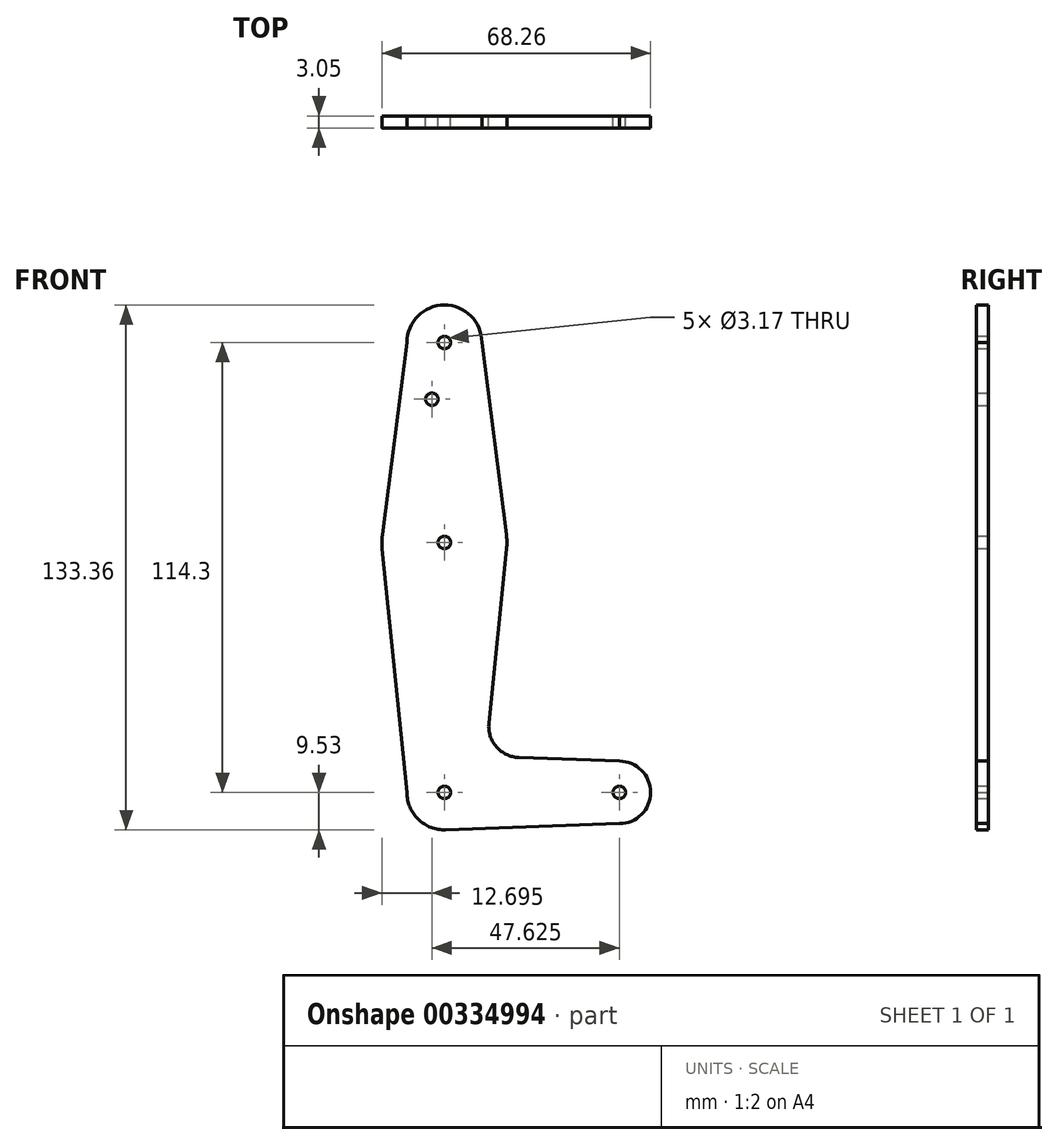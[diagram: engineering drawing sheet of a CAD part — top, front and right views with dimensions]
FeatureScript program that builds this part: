
annotation { "Feature Type Name" : "Feature", "Feature Type Description" : "" }
export const myFeature = defineFeature(function(context is Context, id is Id, definition is map)
    precondition{}
    {
        {
            var Q0;
            Q0=qCreatedBy(makeId("Front.planeOp"),FACE);
            var sketch = newSketch(context, id + "F0", { "sketchPlane" : qUnion([Q0])});
            skLineSegment(sketch, "E0", {"start": v(0, 0) * mm, "end": v(0, 114.3) * mm, "construction": true});
            skCircle(sketch, "E1", {"center": v(0, 114.3) * mm, "radius": 9.53 * mm});
            skCircle(sketch, "E2", {"center": v(0, 63.5) * mm, "radius": 15.88 * mm});
            skLineSegment(sketch, "E3", {"start": v(0, 0) * mm, "end": v(44.45, 0) * mm, "construction": true});
            skCircle(sketch, "E4", {"center": v(0, 0) * mm, "radius": 9.53 * mm});
            skCircle(sketch, "E5", {"center": v(44.45, 0) * mm, "radius": 7.94 * mm});
            skLineSegment(sketch, "E6", {"start": v(-9.53, 114.3) * mm, "end": v(-15.75, 65.5) * mm});
            skLineSegment(sketch, "E7", {"start": v(9.53, 114.3) * mm, "end": v(15.75, 65.5) * mm});
            skLineSegment(sketch, "E8", {"start": v(15.8, 61.9) * mm, "end": v(11.3, 17.6) * mm});
            skCircle(sketch, "E9", {"center": v(-3.18, 99.89) * mm, "radius": 1.59 * mm});
            skCircle(sketch, "E10", {"center": v(0, 114.3) * mm, "radius": 1.59 * mm});
            skCircle(sketch, "E11", {"center": v(0, 63.5) * mm, "radius": 1.59 * mm});
            skCircle(sketch, "E12", {"center": v(0, 0) * mm, "radius": 1.59 * mm});
            skCircle(sketch, "E13", {"center": v(44.45, 0) * mm, "radius": 1.59 * mm});
            skLineSegment(sketch, "E14", {"start": v(44.45, 7.94) * mm, "end": v(18.93, 8.85) * mm});
            skLineSegment(sketch, "E15", {"start": v(44.45, -7.94) * mm, "end": v(0, -9.53) * mm});
            skPoint(sketch, "E16.newPointA", {"position": v(9.53, 0) * mm});
            skArc(sketch, "E16.filletArc", {"start": v(11.3, 17.6) * mm, "mid": v(13.22, 11.57) * mm, "end": v(18.93, 8.85) * mm});
            skLineSegment(sketch, "E17", {"start": v(-15.8, 61.9) * mm, "end": v(-9.52, 0) * mm});
            skSolve(sketch);
        }
        {
            var Q0;
            {var subQ6=sQuery(id+"F0.wireOp",EDGE,"E8");Q0=makeQuery(id+"F0.imprint","IMPRINT",FACE,{"disambiguationData":[TD([[makeQuery(id+"F0.imprint","IMPRINT",EDGE,{"derivedFrom":subQ6}),-1.0]])]});}
            var Q1;
            {var subQ0=sQuery(id+"F0.wireOp",EDGE,"E6");Q1=makeQuery(id+"F0.imprint","IMPRINT",FACE,{"disambiguationData":[TD([[makeQuery(id+"F0.imprint","IMPRINT",EDGE,{"derivedFrom":subQ0}),1.0]])]});}
            var Q2;
            Q2=makeQuery(id+"F0.imprint","IMPRINT",FACE,{"disambiguationData":[TD([[makeQuery(id+"F0.imprint","IMPRINT",EDGE,{"derivedFrom":sQuery(id+"F0.wireOp",EDGE,"E11")}),-1.0]])]});
            var Q3;
            Q3=makeQuery(id+"F0.imprint","IMPRINT",FACE,{"disambiguationData":[TD([[makeQuery(id+"F0.imprint","IMPRINT",EDGE,{"derivedFrom":sQuery(id+"F0.wireOp",EDGE,"E10")}),-1.0]])]});
            var Q4;
            Q4=makeQuery(id+"F0.imprint","IMPRINT",FACE,{"disambiguationData":[TD([[makeQuery(id+"F0.imprint","IMPRINT",EDGE,{"derivedFrom":sQuery(id+"F0.wireOp",EDGE,"E12")}),-1.0]])]});
            var Q5;
            Q5=makeQuery(id+"F0.imprint","IMPRINT",FACE,{"disambiguationData":[TD([[makeQuery(id+"F0.imprint","IMPRINT",EDGE,{"derivedFrom":sQuery(id+"F0.wireOp",EDGE,"E13")}),-1.0]])]});
            extrude(context, id + "F1", {"entities" : qUnion([Q0, Q1, Q2, Q3, Q4, Q5]), "depth" : 3.05 * mm});
        }
    });
